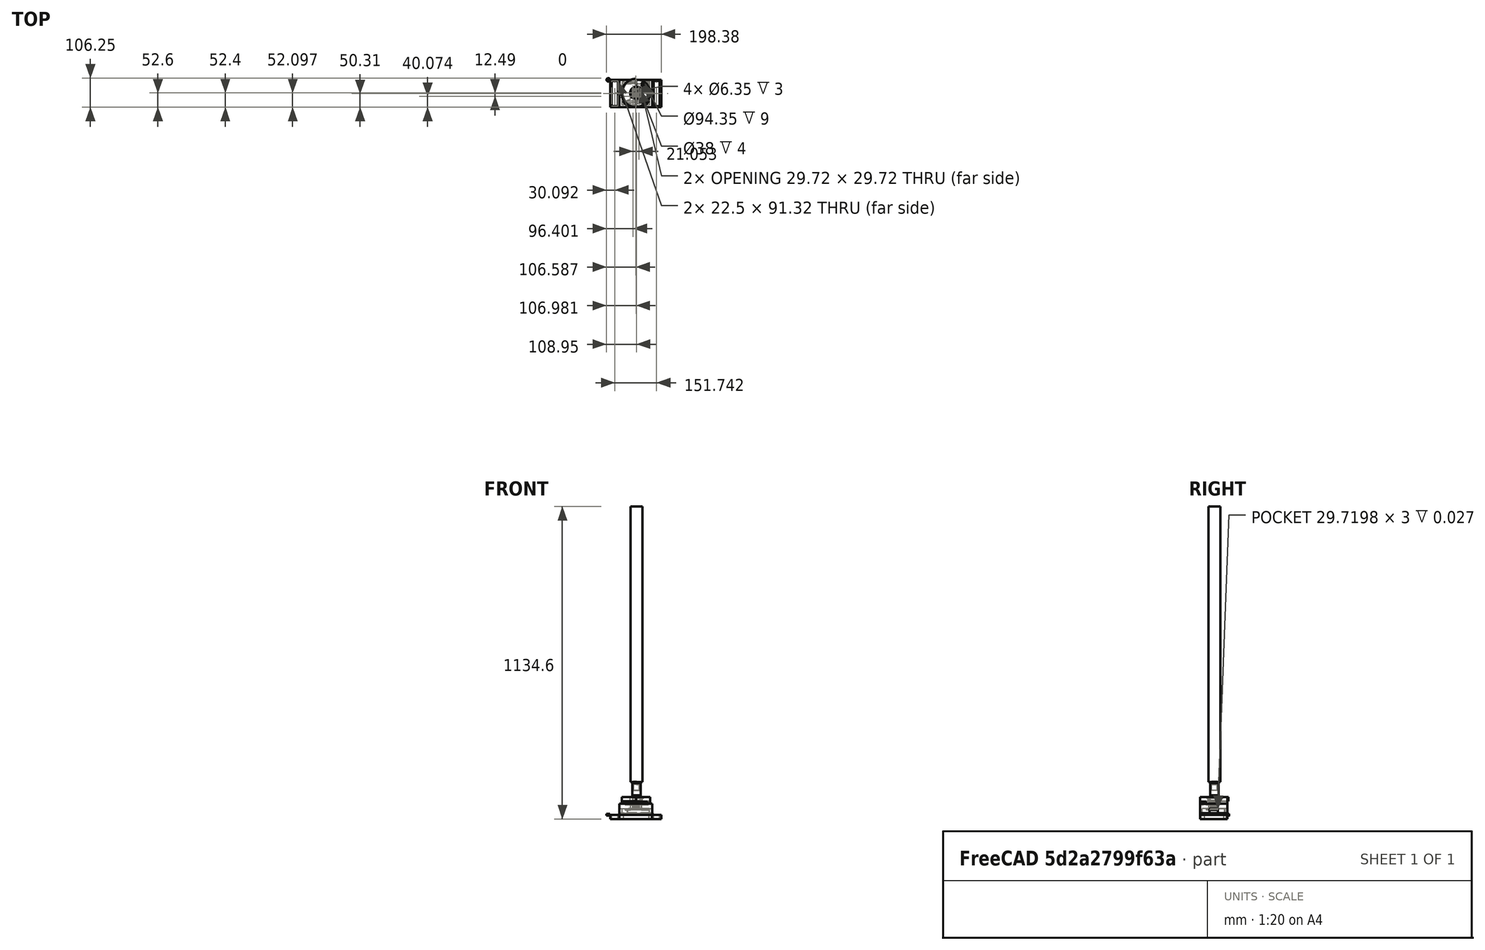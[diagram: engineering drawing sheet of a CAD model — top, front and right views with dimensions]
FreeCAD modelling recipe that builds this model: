
FCSTD DOCUMENT  (FreeCAD 0.20R29603 (Git))
Label: pi_tailtrack_mount
License: All rights reserved
LicenseURL: http://en.wikipedia.org/wiki/All_rights_reserved
objects: Sketcher::SketchObject×43, PartDesign::Pocket×24, PartDesign::Pad×18, Mesh::Feature×13, PartDesign::Body×9, Part::Feature×5, App::MeasureDistance×2, Part::Cut×2, PartDesign::Fillet×1, Part::Compound2×1, PartDesign::FeatureBase×1
note: 146 computed .brp shape members not serialized (recipe doc carries the construction recipe); baked Part::Feature solids carry a one-line shape summary decoded from their .brp

FEATURE [Sketcher::SketchObject] Sketch
  FullyConstrained = false
  MapMode = 5
  Support = -> [XY_Plane]
  sketch-geometry (4):
    g0: LineSegment StartX=0.006331 StartY=0 StartZ=0 EndX=200.006 EndY=0 EndZ=0
    g1: LineSegment StartX=200.006 StartY=0 StartZ=0 EndX=200.006 EndY=-100 EndZ=0
    g2: LineSegment StartX=200.006 StartY=-100 StartZ=0 EndX=0.006331 EndY=-100 EndZ=0
    g3: LineSegment StartX=0.006331 StartY=-100 StartZ=0 EndX=0.006331 EndY=0 EndZ=0
  constraints (13):
    c: Coincident(g0,g1)
    c: Coincident(g1,g2)
    c: Coincident(g2,g3)
    c: Coincident(g3,g0)
    c: Horizontal(g0)
    c: Horizontal(g2)
    c: Vertical(g1)
    c: Vertical(g3)
    c: PointOnObject(g0,g-1)
    c: DistanceX(g0,g0) = 200
    c: DistanceY(g3,g3) = 100
    c: Horizontal(g0,g3)
    c: Horizontal(g3,g-1)
FEATURE [PartDesign::Pad] Pad
  AllowMultiFace = false
  Direction = (0,0,1)
  Length = 6
  Length2 = 100
  Profile = -> Sketch
  Type = 0
FEATURE [Sketcher::SketchObject] Sketch001
  FullyConstrained = false
  MapMode = 5
  Placement = pos=(0,0,6) rot=(0,0,1;0rad)
  Support = -> [Pad]
  sketch-geometry (22):
    g0: LineSegment StartX=0 StartY=0 StartZ=0 EndX=40 EndY=0 EndZ=0
    g1: LineSegment StartX=40 StartY=0 StartZ=0 EndX=40 EndY=-35 EndZ=0
    g2: LineSegment StartX=40 StartY=-35 StartZ=0 EndX=0 EndY=-35 EndZ=0
    g3: LineSegment StartX=0 StartY=-35 StartZ=0 EndX=0 EndY=0 EndZ=0
    g4: LineSegment StartX=0 StartY=-65 StartZ=0 EndX=40 EndY=-65 EndZ=0
    g5: LineSegment StartX=40 StartY=-65 StartZ=0 EndX=40 EndY=-100 EndZ=0
    g6: LineSegment StartX=40 StartY=-100 StartZ=0 EndX=0 EndY=-100 EndZ=0
    g7: LineSegment StartX=0 StartY=-100 StartZ=0 EndX=0 EndY=-65 EndZ=0
    g8: Circle CenterX=19.5564 CenterY=-50 CenterZ=0 NormalX=0 NormalY=0 NormalZ=1 AngleXU=0 Radius=11.9875
    g9: LineSegment StartX=160.311 StartY=0 StartZ=0 EndX=200.311 EndY=0 EndZ=0
    g10: LineSegment StartX=200.311 StartY=0 StartZ=0 EndX=200.311 EndY=-35 EndZ=0
    g11: LineSegment StartX=200.311 StartY=-35 StartZ=0 EndX=160.311 EndY=-35 EndZ=0
    g12: LineSegment StartX=160.311 StartY=-35 StartZ=0 EndX=160.311 EndY=0 EndZ=0
    g13: LineSegment StartX=160.049 StartY=-65 StartZ=0 EndX=200.049 EndY=-65 EndZ=0
    g14: LineSegment StartX=200.049 StartY=-65 StartZ=0 EndX=200.049 EndY=-100 EndZ=0
    g15: LineSegment StartX=200.049 StartY=-100 StartZ=0 EndX=160.049 EndY=-100 EndZ=0
    g16: LineSegment StartX=160.049 StartY=-100 StartZ=0 EndX=160.049 EndY=-65 EndZ=0
    g17: Circle CenterX=179.779 CenterY=-50.3373 CenterZ=0 NormalX=0 NormalY=0 NormalZ=1 AngleXU=0 Radius=11.9875
    g18: LineSegment StartX=53.7678 StartY=-13.6989 StartZ=0 EndX=146 EndY=-13.6989 EndZ=0
    g19: LineSegment StartX=146 StartY=-13.6989 StartZ=0 EndX=146 EndY=-84 EndZ=0
    g20: LineSegment StartX=146 StartY=-84 StartZ=0 EndX=53.7678 EndY=-84 EndZ=0
    g21: LineSegment StartX=53.7678 StartY=-84 StartZ=0 EndX=53.7678 EndY=-13.6989 EndZ=0
  constraints (49):
    c: Coincident(g0,g1)
    c: Coincident(g1,g2)
    c: Coincident(g2,g3)
    c: Coincident(g3,g0)
    c: Horizontal(g0)
    c: Horizontal(g2)
    c: Vertical(g1)
    c: Vertical(g3)
    c: Coincident(g0,g-1)
    c: DistanceX(g0,g0) = 40
    c: DistanceY(g3,g3) = 35
    c: Coincident(g4,g5)
    c: Coincident(g5,g6)
    c: Coincident(g6,g7)
    c: Coincident(g7,g4)
    c: Horizontal(g4)
    c: Horizontal(g6)
    c: Vertical(g5)
    c: Vertical(g7)
    c: Equal(g0,g4) = 40
    c: Equal(g3,g7) = 30
    c: Coincident(g9,g10)
    c: Coincident(g10,g11)
    c: Coincident(g11,g12)
    c: Coincident(g12,g9)
    c: Horizontal(g9)
    c: Horizontal(g11)
    c: Vertical(g10)
    c: Vertical(g12)
    c: Equal(g0,g9) = 40
    c: Equal(g3,g12) = 35
    c: Coincident(g13,g14)
    c: Coincident(g14,g15)
    c: Coincident(g15,g16)
    c: Coincident(g16,g13)
    c: Horizontal(g13)
    c: Horizontal(g15)
    c: Vertical(g14)
    c: Vertical(g16)
    c: Equal(g9,g13) = 40
    c: Equal(g12,g16) = 30
    c: Coincident(g18,g19)
    c: Coincident(g19,g20)
    c: Coincident(g20,g21)
    c: Coincident(g21,g18)
    c: Horizontal(g18)
    c: Horizontal(g20)
    c: Vertical(g19)
    c: Vertical(g21)
FEATURE [PartDesign::Pocket] Pocket
  AllowMultiFace = false
  BaseFeature = -> Pad
  Direction = (1,1,1)
  Length = 6
  Length2 = 100
  Profile = -> Sketch001
  Type = 0
FEATURE [Sketcher::SketchObject] Sketch002
  FullyConstrained = false
  MapMode = 5
  Placement = pos=(0,0,6) rot=(0,0,1;0rad)
  Support = -> [Pocket]
  sketch-geometry (16):
    g0: LineSegment StartX=40 StartY=-35.1993 StartZ=0 EndX=40 EndY=0 EndZ=0
    g1: LineSegment StartX=40 StartY=0 StartZ=0 EndX=160 EndY=0 EndZ=0
    g2: LineSegment StartX=160 StartY=0 StartZ=0 EndX=160 EndY=-35 EndZ=0
    g3: LineSegment StartX=160 StartY=-35 StartZ=0 EndX=149.235 EndY=-35 EndZ=0
    g4: LineSegment StartX=149.235 StartY=-35 StartZ=0 EndX=149.235 EndY=-8.23021 EndZ=0
    g5: LineSegment StartX=149.235 StartY=-8.23021 StartZ=0 EndX=50.0613 EndY=-8.23021 EndZ=0
    g6: LineSegment StartX=50.0613 StartY=-8.23021 StartZ=0 EndX=50.0613 EndY=-35.1993 EndZ=0
    g7: LineSegment StartX=50.0613 StartY=-35.1993 StartZ=0 EndX=40 EndY=-35.1993 EndZ=0
    g8: LineSegment StartX=40 StartY=-100 StartZ=0 EndX=160 EndY=-100 EndZ=0
    g9: LineSegment StartX=160 StartY=-100 StartZ=0 EndX=160 EndY=-65 EndZ=0
    g10: LineSegment StartX=160 StartY=-65 StartZ=0 EndX=149.545 EndY=-65 EndZ=0
    g11: LineSegment StartX=149.545 StartY=-65 StartZ=0 EndX=149.545 EndY=-91.5759 EndZ=0
    g12: LineSegment StartX=149.545 StartY=-91.5759 StartZ=0 EndX=50.3566 EndY=-91.5759 EndZ=0
    g13: LineSegment StartX=50.3566 StartY=-91.5759 StartZ=0 EndX=50.3566 EndY=-65 EndZ=0
    g14: LineSegment StartX=50.3566 StartY=-65 StartZ=0 EndX=40 EndY=-65 EndZ=0
    g15: LineSegment StartX=40 StartY=-65 StartZ=0 EndX=40 EndY=-100 EndZ=0
  constraints (31):
    c: Vertical(g0)
    c: Coincident(g0,g1)
    c: Horizontal(g1)
    c: Coincident(g1,g2)
    c: Vertical(g2)
    c: Coincident(g2,g3)
    c: Horizontal(g3)
    c: Coincident(g3,g4)
    c: Vertical(g4)
    c: Coincident(g4,g5)
    c: Horizontal(g5)
    c: Coincident(g5,g6)
    c: Vertical(g6)
    c: Coincident(g6,g7)
    c: Coincident(g7,g0)
    c: Horizontal(g7)
    c: Horizontal(g8)
    c: Coincident(g8,g9)
    c: Vertical(g9)
    c: Coincident(g9,g10)
    c: Horizontal(g10)
    c: Coincident(g10,g11)
    c: Vertical(g11)
    c: Coincident(g11,g12)
    c: Horizontal(g12)
    c: Coincident(g12,g13)
    c: Vertical(g13)
    c: Coincident(g13,g14)
    c: Coincident(g14,g15)
    c: Coincident(g15,g8)
    c: Vertical(g15)
FEATURE [PartDesign::Pad] Pad001
  AllowMultiFace = false
  BaseFeature = -> Pocket
  Direction = (0,0,1)
  Length = 34
  Length2 = 100
  Profile = -> Sketch002
  Type = 0
FEATURE [Sketcher::SketchObject] Sketch003
  FullyConstrained = false
  MapMode = 5
  Placement = pos=(0,0,40) rot=(0,0,1;0rad)
  Support = -> [Pad001]
  sketch-geometry (4):
    g0: LineSegment StartX=40 StartY=-0.238451 StartZ=0 EndX=160 EndY=-0.238451 EndZ=0
    g1: LineSegment StartX=160 StartY=-0.238451 StartZ=0 EndX=160 EndY=-100 EndZ=0
    g2: LineSegment StartX=160 StartY=-100 StartZ=0 EndX=40 EndY=-100 EndZ=0
    g3: LineSegment StartX=40 StartY=-100 StartZ=0 EndX=40 EndY=-0.238451 EndZ=0
  constraints (8):
    c: Coincident(g0,g1)
    c: Coincident(g1,g2)
    c: Coincident(g2,g3)
    c: Coincident(g3,g0)
    c: Horizontal(g0)
    c: Horizontal(g2)
    c: Vertical(g1)
    c: Vertical(g3)
FEATURE [PartDesign::Pad] Pad002
  AllowMultiFace = false
  BaseFeature = -> Pad001
  Direction = (0,0,1)
  Length = 18
  Length2 = 100
  Profile = -> Sketch003
  Reversed = true
  Type = 0
FEATURE [Sketcher::SketchObject] Sketch004
  FullyConstrained = false
  MapMode = 5
  Placement = pos=(0,0,40) rot=(0,0,1;0rad)
  Support = -> [Pad002]
  sketch-geometry (4):
    g0: LineSegment StartX=82.7298 StartY=-35 StartZ=0 EndX=118.25 EndY=-35 EndZ=0
    g1: LineSegment StartX=118.25 StartY=-35 StartZ=0 EndX=118.25 EndY=-64.9692 EndZ=0
    g2: LineSegment StartX=118.25 StartY=-64.9692 StartZ=0 EndX=82.7298 EndY=-64.9692 EndZ=0
    g3: LineSegment StartX=82.7298 StartY=-64.9692 StartZ=0 EndX=82.7298 EndY=-35 EndZ=0
  constraints (9):
    c: Coincident(g0,g1)
    c: Coincident(g1,g2)
    c: Coincident(g2,g3)
    c: Coincident(g3,g0)
    c: Horizontal(g0)
    c: Horizontal(g2)
    c: Vertical(g1)
    c: Vertical(g3)
    c: DistanceX(g0,g0) = 35.52
FEATURE [PartDesign::Pocket] Pocket001
  AllowMultiFace = false
  BaseFeature = -> Pad002
  Direction = (1,1,1)
  Length = 5
  Length2 = 100
  Profile = -> Sketch004
  Type = 0
FEATURE [Sketcher::SketchObject] Sketch005
  FullyConstrained = false
  MapMode = 5
  Placement = pos=(0,0,35) rot=(0,0,1;0rad)
  Support = -> [Pocket001]
  sketch-geometry (9):
    g0: Circle CenterX=90.1364 CenterY=-47.5 CenterZ=0 NormalX=0 NormalY=0 NormalZ=1 AngleXU=0 Radius=1.5
    g1: Circle CenterX=111.136 CenterY=-47.5 CenterZ=0 NormalX=0 NormalY=0 NormalZ=1 AngleXU=0 Radius=1.5
    g2: Circle CenterX=90.1364 CenterY=-60 CenterZ=0 NormalX=0 NormalY=0 NormalZ=1 AngleXU=0 Radius=1.5
    g3: Circle CenterX=111.136 CenterY=-60 CenterZ=0 NormalX=0 NormalY=0 NormalZ=1 AngleXU=0 Radius=1.5
    g4: LineSegment StartX=105.584 StartY=-52.4517 StartZ=0 EndX=105.588 EndY=-42.5522 EndZ=0
    g5: LineSegment StartX=105.588 StartY=-42.5522 StartZ=0 EndX=95.6887 EndY=-42.5483 EndZ=0
    g6: LineSegment StartX=95.6887 StartY=-42.5483 StartZ=0 EndX=95.6847 EndY=-52.4478 EndZ=0
    g7: LineSegment StartX=95.6847 StartY=-52.4478 StartZ=0 EndX=105.584 EndY=-52.4517 EndZ=0
    g8: Circle CenterX=100.636 CenterY=-47.5 CenterZ=0 NormalX=0 NormalY=0 NormalZ=1 AngleXU=0 Radius=7
  constraints (24):
    c: Radius(g0) = 1.5
    c: Equal(g0,g1) = 2.2
    c: Horizontal(g1,g0)
    c: DistanceX(g0,g1) = 21
    c: Equal(g0,g2) = 2.2
    c: Equal(g2,g3) = 2.2
    c: Horizontal(g3,g2)
    c: DistanceX(g2,g3) = 21
    c: Vertical(g1,g3)
    c: DistanceY(g3,g1) = 12.5
    c: Coincident(g4,g5)
    c: Coincident(g5,g6)
    c: Coincident(g6,g7)
    c: Coincident(g7,g4)
    c: Equal(g4,g5)
    c: Equal(g4,g6)
    c: Equal(g4,g7)
    c: PointOnObject(g4,g8)
    c: PointOnObject(g5,g8)
    c: PointOnObject(g6,g8)
    c: PointOnObject(g7,g8)
    c: Horizontal(g8,g1)
    c: Radius(g8) = 7
    c: DistanceX(g8,g1) = 10.5
FEATURE [PartDesign::Pocket] Pocket002
  AllowMultiFace = false
  BaseFeature = -> Pocket001
  Direction = (1,1,1)
  Length = 20
  Length2 = 100
  Profile = -> Sketch005
  Type = 0
FEATURE [Sketcher::SketchObject] Sketch007
  FullyConstrained = false
  MapMode = 5
  Placement = pos=(0,0,35) rot=(0,0,1;0rad)
  Support = -> [Pocket002]
  sketch-geometry (1):
    g0: Circle CenterX=100.615 CenterY=-47.5274 CenterZ=0 NormalX=0 NormalY=0 NormalZ=1 AngleXU=0 Radius=7
  constraints (1):
    c: Radius(g0) = 7
FEATURE [PartDesign::Pocket] Pocket003
  AllowMultiFace = false
  BaseFeature = -> Pocket002
  Direction = (1,1,1)
  Length = 7
  Length2 = 100
  Profile = -> Sketch007
  Type = 0
FEATURE [Sketcher::SketchObject] Sketch008
  FullyConstrained = false
  MapMode = 5
  Placement = pos=(0,0,0) rot=(0,0.707107,0.707107;3.14159rad)
  Support = -> [Pocket003]
  sketch-geometry (4):
    g0: LineSegment StartX=-150.026 StartY=23.0402 StartZ=0 EndX=-69.393 EndY=23.0402 EndZ=0
    g1: LineSegment StartX=-69.393 StartY=23.0402 StartZ=0 EndX=-69.393 EndY=7.47677 EndZ=0
    g2: LineSegment StartX=-69.393 StartY=7.47677 StartZ=0 EndX=-150.026 EndY=7.47677 EndZ=0
    g3: LineSegment StartX=-150.026 StartY=7.47677 StartZ=0 EndX=-150.026 EndY=23.0402 EndZ=0
  constraints (8):
    c: Coincident(g0,g1)
    c: Coincident(g1,g2)
    c: Coincident(g2,g3)
    c: Coincident(g3,g0)
    c: Horizontal(g0)
    c: Horizontal(g2)
    c: Vertical(g1)
    c: Vertical(g3)
FEATURE [PartDesign::Pocket] Pocket004
  AllowMultiFace = false
  BaseFeature = -> Pocket003
  Direction = (1,1,1)
  Length = 10
  Length2 = 100
  Profile = -> Sketch008
  Type = 0
FEATURE [Sketcher::SketchObject] Sketch015
  FullyConstrained = false
  MapMode = 5
  Placement = pos=(0,0,22) rot=(1,0,0;3.14159rad)
  sketch-geometry (4):
    g0: LineSegment StartX=91.912 StartY=65.7684 StartZ=0 EndX=109.419 EndY=65.7684 EndZ=0
    g1: LineSegment StartX=109.419 StartY=65.7684 StartZ=0 EndX=109.419 EndY=42.0857 EndZ=0
    g2: LineSegment StartX=109.419 StartY=42.0857 StartZ=0 EndX=91.912 EndY=42.0857 EndZ=0
    g3: LineSegment StartX=91.912 StartY=42.0857 StartZ=0 EndX=91.912 EndY=65.7684 EndZ=0
  constraints (8):
    c: Coincident(g0,g1)
    c: Coincident(g1,g2)
    c: Coincident(g2,g3)
    c: Coincident(g3,g0)
    c: Horizontal(g0)
    c: Horizontal(g2)
    c: Vertical(g1)
    c: Vertical(g3)
FEATURE [PartDesign::Pocket] Pocket006
  AllowMultiFace = false
  BaseFeature = -> Pocket004
  Direction = (1,1,1)
  Length = 5
  Length2 = 100
  Profile = -> Sketch015
  Type = 0
FEATURE [Sketcher::SketchObject] Sketch017
  FullyConstrained = false
  MapMode = 5
  Placement = pos=(0,0,40) rot=(0,0,1;0rad)
  Support = -> [Pocket006]
  sketch-geometry (30):
    g0: LineSegment StartX=100.494 StartY=-47.5573 StartZ=0 EndX=59.1615 EndY=-80.1273 EndZ=0
    g1: LineSegment StartX=59.1615 StartY=-80.1273 StartZ=0 EndX=63.9045 EndY=-85.2755 EndZ=0
    g2: LineSegment StartX=63.9045 StartY=-85.2755 StartZ=0 EndX=100.494 EndY=-47.5573 EndZ=0
    g3: LineSegment StartX=100.494 StartY=-47.5573 StartZ=0 EndX=65.7209 EndY=-86.1298 EndZ=0
    g4: LineSegment StartX=65.7209 StartY=-86.1298 StartZ=0 EndX=70.9953 EndY=-90.7321 EndZ=0
    g5: LineSegment StartX=70.9953 StartY=-90.7321 StartZ=0 EndX=100.494 EndY=-47.5573 EndZ=0
    g6: LineSegment StartX=100.469 StartY=-47.6647 StartZ=0 EndX=72.3164 EndY=-91.783 EndZ=0
    g7: LineSegment StartX=72.3164 StartY=-91.783 StartZ=0 EndX=78.3711 EndY=-95.2959 EndZ=0
    g8: LineSegment StartX=78.3711 StartY=-95.2959 StartZ=0 EndX=100.469 EndY=-47.6647 EndZ=0
    g9: LineSegment StartX=100.574 StartY=-47.6121 StartZ=0 EndX=80.8298 EndY=-96.4275 EndZ=0
    g10: LineSegment StartX=80.8298 StartY=-96.4275 StartZ=0 EndX=87.4364 EndY=-98.7413 EndZ=0
    g11: LineSegment StartX=87.4364 StartY=-98.7413 StartZ=0 EndX=100.574 EndY=-47.6121 EndZ=0
    g12: LineSegment StartX=100.574 StartY=-47.6121 StartZ=0 EndX=109.54 EndY=-99.3646 EndZ=0
    g13: LineSegment StartX=109.54 StartY=-99.3646 StartZ=0 EndX=116.439 EndY=-98.178 EndZ=0
    g14: LineSegment StartX=116.439 StartY=-98.178 StartZ=0 EndX=100.574 EndY=-47.6121 EndZ=0
    g15: LineSegment StartX=100.469 StartY=-47.6647 StartZ=0 EndX=100.478 EndY=-100.164 EndZ=0
    g16: LineSegment StartX=100.478 StartY=-100.164 StartZ=0 EndX=107.473 EndY=-99.8814 EndZ=0
    g17: LineSegment StartX=107.473 StartY=-99.8814 StartZ=0 EndX=100.469 EndY=-47.6647 EndZ=0
    g18: LineSegment StartX=100.494 StartY=-47.5573 StartZ=0 EndX=126.724 EndY=-94.2924 EndZ=0
    g19: LineSegment StartX=126.724 StartY=-94.2924 StartZ=0 EndX=132.437 EndY=-90.2469 EndZ=0
    g20: LineSegment StartX=132.437 StartY=-90.2469 StartZ=0 EndX=100.494 EndY=-47.5573 EndZ=0
    g21: LineSegment StartX=100.494 StartY=-47.5573 StartZ=0 EndX=118.389 EndY=-97.4537 EndZ=0
    g22: LineSegment StartX=118.389 StartY=-97.4537 StartZ=0 EndX=124.92 EndY=-94.9352 EndZ=0
    g23: LineSegment StartX=124.92 StartY=-94.9352 StartZ=0 EndX=100.494 EndY=-47.5573 EndZ=0
    g24: LineSegment StartX=100.512 StartY=-47.5427 StartZ=0 EndX=134.392 EndY=-88.2304 EndZ=0
    g25: LineSegment StartX=134.392 StartY=-88.2304 StartZ=0 EndX=139.543 EndY=-83.3947 EndZ=0
    g26: LineSegment StartX=139.543 StartY=-83.3947 StartZ=0 EndX=100.512 EndY=-47.5427 EndZ=0
    g27: LineSegment StartX=100.378 StartY=-47.7964 StartZ=0 EndX=90.0278 EndY=-99.6655 EndZ=0
    g28: LineSegment StartX=97.5884 StartY=-100.124 StartZ=0 EndX=100.378 EndY=-47.7964 EndZ=0
    g29: LineSegment StartX=90.0278 StartY=-99.6655 StartZ=0 EndX=97.5884 EndY=-100.124 EndZ=0
  constraints (35):
    c: Coincident(g0,g1)
    c: Coincident(g1,g2)
    c: Coincident(g2,g0)
    c: Distance(g1) = 7
    c: Coincident(g3,g4)
    c: Coincident(g4,g5)
    c: Coincident(g5,g3)
    c: Equal(g1,g4) = 7
    c: Coincident(g6,g7)
    c: Coincident(g7,g8)
    c: Coincident(g8,g6)
    c: Equal(g1,g7) = 7
    c: Coincident(g9,g10)
    c: Coincident(g10,g11)
    c: Coincident(g11,g9)
    c: Equal(g7,g10) = 7
    c: Coincident(g12,g13)
    c: Coincident(g13,g14)
    c: Coincident(g14,g12)
    c: Coincident(g15,g16)
    c: Coincident(g16,g17)
    c: Coincident(g17,g15)
    c: Coincident(g18,g19)
    c: Coincident(g19,g20)
    c: Coincident(g20,g18)
    c: Equal(g16,g19) = 7
    c: Coincident(g21,g22)
    c: Coincident(g22,g23)
    c: Coincident(g23,g21)
    c: Coincident(g24,g25)
    c: Coincident(g25,g26)
    c: Coincident(g26,g24)
    c: Coincident(g27,g29)
    c: Coincident(g29,g28)
    c: Coincident(g28,g27)
FEATURE [Sketcher::SketchObject] Sketch024
  FullyConstrained = false
  MapMode = 5
  Support = -> [XY_Plane001]
  sketch-geometry (2):
    g0: Circle CenterX=100.523 CenterY=-47.941 CenterZ=0 NormalX=0 NormalY=0 NormalZ=1 AngleXU=0 Radius=51.2787
    g1: Circle CenterX=100.523 CenterY=-47.941 CenterZ=0 NormalX=0 NormalY=0 NormalZ=1 AngleXU=0 Radius=21.439
  constraints (1):
    c: Coincident(g1,g0)
FEATURE [PartDesign::Pad] Pad006
  AllowMultiFace = false
  Direction = (0,0,1)
  Length = 16
  Length2 = 100
  Profile = -> Sketch024
  Type = 0
FEATURE [Sketcher::SketchObject] Sketch025
  FullyConstrained = false
  MapMode = 5
  Placement = pos=(0,0,16) rot=(0,0,1;0rad)
  Support = -> [Pad006]
  sketch-geometry (4):
    g0: LineSegment StartX=100.838 StartY=17.0552 StartZ=0 EndX=167.008 EndY=17.0552 EndZ=0
    g1: LineSegment StartX=167.008 StartY=17.0552 StartZ=0 EndX=167.008 EndY=-112.472 EndZ=0
    g2: LineSegment StartX=167.008 StartY=-112.472 StartZ=0 EndX=100.838 EndY=-112.472 EndZ=0
    g3: LineSegment StartX=100.838 StartY=-112.472 StartZ=0 EndX=100.838 EndY=17.0552 EndZ=0
  constraints (8):
    c: Coincident(g0,g1)
    c: Coincident(g1,g2)
    c: Coincident(g2,g3)
    c: Coincident(g3,g0)
    c: Horizontal(g0)
    c: Horizontal(g2)
    c: Vertical(g1)
    c: Vertical(g3)
FEATURE [PartDesign::Pocket] Pocket011
  AllowMultiFace = false
  BaseFeature = -> Pad006
  Direction = (0,0,-1)
  Length = 16
  Length2 = 100
  Profile = -> Sketch025
  Type = 0
FEATURE [PartDesign::Body] Body001  label="Semicircle"
  Group = -> [Sketch024,Pad006,Sketch025,Pocket011]
  Origin = -> Origin001
  Placement = pos=(0,0,49) rot=(0,0,1;0rad)
  Tip = -> Pocket011
FEATURE [Sketcher::SketchObject] Sketch030
  FullyConstrained = false
  MapMode = 5
  Support = -> [XY_Plane002]
  sketch-geometry (1):
    g0: Circle CenterX=124.126 CenterY=-13.6891 CenterZ=0 NormalX=0 NormalY=0 NormalZ=1 AngleXU=0 Radius=3.26461
FEATURE [PartDesign::Pad] Pad009
  AllowMultiFace = false
  Direction = (1,1,1)
  Length = 50
  Length2 = 100
  Profile = -> Sketch030
  Type = 0
FEATURE [PartDesign::Body] Body002  label="LeftEyeCut"
  Group = -> [Sketch030,Pad009]
  Origin = -> Origin002
  Placement = pos=(2,-5,98) rot=(-0.707107,0.707107,0;0.785398rad)
  Tip = -> Pad009
FEATURE [Sketcher::SketchObject] Sketch031
  FullyConstrained = false
  MapMode = 5
  Support = -> [XY_Plane003]
  sketch-geometry (1):
    g0: Circle CenterX=124.126 CenterY=-13.6891 CenterZ=0 NormalX=0 NormalY=0 NormalZ=1 AngleXU=0 Radius=3.26461
FEATURE [PartDesign::Pad] Pad010
  AllowMultiFace = false
  Direction = (1,1,1)
  Length = 50
  Length2 = 100
  Profile = -> Sketch031
  Type = 0
FEATURE [PartDesign::Body] Body003  label="RigthEyeCut"
  Group = -> [Sketch031,Pad010]
  Origin = -> Origin003
  Placement = pos=(6,-65,112) rot=(0.707107,0.707107,0;0.785398rad)
  Tip = -> Pad010
FEATURE [Sketcher::SketchObject] Sketch032
  FullyConstrained = false
  MapMode = 5
  Support = -> [XY_Plane004]
  sketch-geometry (4):
    g0: LineSegment StartX=82.7935 StartY=-35.0406 StartZ=0 EndX=118.134 EndY=-35.0406 EndZ=0
    g1: LineSegment StartX=118.134 StartY=-35.0406 StartZ=0 EndX=118.134 EndY=-64.7316 EndZ=0
    g2: LineSegment StartX=118.134 StartY=-64.7316 StartZ=0 EndX=82.7935 EndY=-64.7316 EndZ=0
    g3: LineSegment StartX=82.7935 StartY=-64.7316 StartZ=0 EndX=82.7935 EndY=-35.0406 EndZ=0
  constraints (8):
    c: Coincident(g0,g1)
    c: Coincident(g1,g2)
    c: Coincident(g2,g3)
    c: Coincident(g3,g0)
    c: Horizontal(g0)
    c: Horizontal(g2)
    c: Vertical(g1)
    c: Vertical(g3)
FEATURE [PartDesign::Pad] Pad011
  AllowMultiFace = false
  Direction = (1,1,1)
  Length = 5
  Length2 = 100
  Profile = -> Sketch032
  Type = 0
FEATURE [Sketcher::SketchObject] Sketch033
  FullyConstrained = false
  MapMode = 5
  Placement = pos=(0,0,0) rot=(1,0,0;3.14159rad)
  Support = -> [Pad011]
  sketch-geometry (4):
    g0: Circle CenterX=90.1511 CenterY=59.9051 CenterZ=0 NormalX=0 NormalY=0 NormalZ=1 AngleXU=0 Radius=3.17621
    g1: Circle CenterX=90.237 CenterY=47.4366 CenterZ=0 NormalX=0 NormalY=0 NormalZ=1 AngleXU=0 Radius=3.17621
    g2: Circle CenterX=111.204 CenterY=59.9265 CenterZ=0 NormalX=0 NormalY=0 NormalZ=1 AngleXU=0 Radius=3.17621
    g3: Circle CenterX=111.204 CenterY=47.501 CenterZ=0 NormalX=0 NormalY=0 NormalZ=1 AngleXU=0 Radius=3.17621
FEATURE [PartDesign::Pocket] Pocket014
  AllowMultiFace = false
  BaseFeature = -> Pad011
  Direction = (1,1,1)
  Length = 3
  Length2 = 100
  Profile = -> Sketch033
  Type = 0
FEATURE [Sketcher::SketchObject] Sketch034
  FullyConstrained = false
  MapMode = 5
  Placement = pos=(0,0,0) rot=(1,0,0;3.14159rad)
  Support = -> [Pocket014]
  sketch-geometry (1):
    g0: Circle CenterX=100.582 CenterY=47.4887 CenterZ=0 NormalX=0 NormalY=0 NormalZ=1 AngleXU=0 Radius=7
  constraints (1):
    c: Diameter(g0) = 14
FEATURE [PartDesign::Pocket] Pocket015
  AllowMultiFace = false
  BaseFeature = -> Pocket014
  Direction = (1,1,1)
  Length = 5
  Length2 = 100
  Profile = -> Sketch034
  Type = 0
FEATURE [PartDesign::Body] Body004  label="CameraDepressionInsert"
  Group = -> [Sketch032,Pad011,Sketch033,Pocket014,Sketch034,Pocket015]
  Origin = -> Origin004
  Placement = pos=(0,0,35) rot=(0,0,1;0rad)
  Tip = -> Pocket015
FEATURE [Part::Feature] Part__Feature  label="Cam V2.1 v1"
  Placement = pos=(100.6,-50,21) rot=(0.707107,0,0.707107;3.14159rad)
  shape: bbox 25 x 24 x 6.45 mm, 247 faces (baked)
FEATURE [Mesh::Feature] LED_5mm  label="Red_LED_1"
  Placement = pos=(135.001,0.727905,87.6792) rot=(0.962528,-0.0838,-0.257909;2.53538rad)
FEATURE [Mesh::Feature] LED_5mm001  label="Red_LED_2"
  Placement = pos=(133.359,-85.3415,94.0713) rot=(0.948002,-0.161603,-0.274184;3.58891rad)
FEATURE [Mesh::Feature] LED_5mm002  label="IR_LED"
  Placement = pos=(154.892,-115.515,46.8) rot=(-0.873594,-0.344118,0.344118;1.70553rad)
FEATURE [Mesh::Feature] LED_5mm003  label="IR_LED001"
  Placement = pos=(142.243,-124.48,46.8) rot=(-0.922341,-0.27321,0.27321;1.65155rad)
FEATURE [Mesh::Feature] LED_5mm004  label="IR_LED002"
  Placement = pos=(128.505,-130.552,46.8) rot=(-0.961012,-0.19552,0.19552;1.61055rad)
FEATURE [Mesh::Feature] LED_5mm005  label="IR_LED003"
  Placement = pos=(114.514,-134.49,46.8) rot=(-0.985257,-0.120974,0.120974;1.58565rad)
FEATURE [Mesh::Feature] LED_5mm006  label="IR_LED004"
  Placement = pos=(99.6109,-135.395,46.8) rot=(-0.998783,-0.034878,0.034878;1.57201rad)
FEATURE [Mesh::Feature] LED_5mm007  label="IR_LED005"
  Placement = pos=(82.8154,-133.75,46.8) rot=(-0.99628,0.060935,-0.060935;1.57452rad)
FEATURE [Mesh::Feature] LED_5mm008  label="IR_LED006"
  Placement = pos=(64.7966,-127.636,46.8) rot=(-0.967324,0.179283,-0.179283;1.60401rad)
FEATURE [Mesh::Feature] LED_5mm009  label="IR_LED007"
  Placement = pos=(51.4171,-120.378,46.8) rot=(-0.935113,0.250563,-0.250563;1.63783rad)
FEATURE [Mesh::Feature] LED_5mm010  label="IR_LED008"
  Placement = pos=(40.3946,-111.928,46.8) rot=(-0.894141,0.316632,-0.316632;1.68246rad)
FEATURE [Mesh::Feature] LED_5mm011  label="IR_LED009"
  Placement = pos=(30.1096,-100.339,46.8) rot=(-0.834817,0.389282,-0.389282;1.75037rad)
FEATURE [Part::Feature] Part__Feature001  label="TTN031489-E0W"
  Placement = pos=(102.7,-47.4,82.1) rot=(0,1,0;1.5708rad)
  shape: bbox 29.97 x 29.97 x 78.87 mm, 81 faces (baked)
FEATURE [Mesh::Feature] Zebrafish_6dpf_actualActualSize  label="Zebrafish-6dpf-actualActualSize"
  Placement = pos=(102.4,-47.5,41.6) rot=(0.57735,0.57735,0.57735;2.0944rad)
FEATURE [Sketcher::SketchObject] Sketch035
  FullyConstrained = false
  MapMode = 5
  Support = -> [XY_Plane005]
  sketch-geometry (1):
    g0: Circle CenterX=100.659 CenterY=-47.5423 CenterZ=0 NormalX=0 NormalY=0 NormalZ=1 AngleXU=0 Radius=20
  constraints (1):
    c: Diameter(g0) = 40
FEATURE [PartDesign::Pad] Pad012
  Direction = (0,0,1)
  Length = 1
  Length2 = 10
  Profile = -> Sketch035
  Type = 0
FEATURE [Sketcher::SketchObject] Sketch036
  FullyConstrained = false
  MapMode = 5
  Placement = pos=(0,0,1) rot=(0,0,1;0rad)
  Support = -> [Pad012]
  sketch-geometry (2):
    g0: Circle CenterX=100.731 CenterY=-47.6003 CenterZ=0 NormalX=0 NormalY=0 NormalZ=1 AngleXU=0 Radius=20
    g1: Circle CenterX=100.731 CenterY=-47.6003 CenterZ=0 NormalX=0 NormalY=0 NormalZ=1 AngleXU=0 Radius=19
  constraints (3):
    c: Diameter(g0) = 40
    c: Coincident(g1,g0)
    c: Diameter(g1) = 38
FEATURE [PartDesign::Pad] Pad013
  BaseFeature = -> Pad012
  Direction = (0,0,1)
  Length = 4
  Length2 = 10
  Profile = -> Sketch036
  Type = 0
FEATURE [PartDesign::Body] Body005  label="40mm_dish"
  Group = -> [Sketch035,Pad012,Sketch036,Pad013]
  Origin = -> Origin005
  Placement = pos=(0,0,40) rot=(0,0,1;0rad)
  Tip = -> Pad013
FEATURE [Sketcher::SketchObject] Sketch037
  FullyConstrained = false
  MapMode = 5
  Support = -> [XY_Plane006]
  sketch-geometry (1):
    g0: Circle CenterX=102.61 CenterY=-47.5813 CenterZ=0 NormalX=0 NormalY=0 NormalZ=1 AngleXU=0 Radius=7.5
  constraints (1):
    c: Diameter(g0) = 15
FEATURE [PartDesign::Pad] Pad014
  Direction = (0,0,1)
  Length = 2
  Length2 = 10
  Profile = -> Sketch037
  Type = 0
FEATURE [PartDesign::Fillet] Fillet
  Base = -> Pad014 [Face3]
  BaseFeature = -> Pad014
  Radius = 1.9
  SupportTransform = false
  UseAllEdges = false
FEATURE [Sketcher::SketchObject] Sketch038
  FullyConstrained = false
  MapMode = 5
  Placement = pos=(0,0,2) rot=(0,0,1;0rad)
  Support = -> [Fillet]
  sketch-geometry (4):
    g0: LineSegment StartX=93.544 StartY=-43.374 StartZ=0 EndX=101.094 EndY=-43.374 EndZ=0
    g1: LineSegment StartX=101.094 StartY=-43.374 StartZ=0 EndX=101.094 EndY=-52.0559 EndZ=0
    g2: LineSegment StartX=101.094 StartY=-52.0559 StartZ=0 EndX=93.544 EndY=-52.0559 EndZ=0
    g3: LineSegment StartX=93.544 StartY=-52.0559 StartZ=0 EndX=93.544 EndY=-43.374 EndZ=0
  constraints (8):
    c: Coincident(g0,g1)
    c: Coincident(g1,g2)
    c: Coincident(g2,g3)
    c: Coincident(g3,g0)
    c: Horizontal(g0)
    c: Horizontal(g2)
    c: Vertical(g1)
    c: Vertical(g3)
FEATURE [PartDesign::Pocket] Pocket016
  BaseFeature = -> Fillet
  Direction = (1,1,1)
  Length = 5
  Length2 = 5
  Profile = -> Sketch038
  Type = 0
FEATURE [PartDesign::Body] Body006  label="Agarose_block"
  Group = -> [Sketch037,Pad014,Fillet,Sketch038,Pocket016]
  Origin = -> Origin006
  Placement = pos=(0,0,40) rot=(0,0,1;0rad)
  Tip = -> Pocket016
FEATURE [Sketcher::SketchObject] Sketch039
  FullyConstrained = false
  MapMode = 5
  Support = -> [XY_Plane007]
  sketch-geometry (1):
    g0: Circle CenterX=102.568 CenterY=-47.0303 CenterZ=0 NormalX=0 NormalY=0 NormalZ=1 AngleXU=0 Radius=21.6315
FEATURE [PartDesign::Pad] Pad015
  Direction = (0,0,1)
  Length = 1000
  Length2 = 10
  Profile = -> Sketch039
  Type = 0
FEATURE [PartDesign::Body] Body007  label="MicroscopeTube"
  Group = -> [Sketch039,Pad015]
  Origin = -> Origin007
  Placement = pos=(0,0,119.6) rot=(0,0,1;0rad)
  Tip = -> Pad015
FEATURE [Part::Feature] Solid002
  shape: bbox 12.5 x 12.5 x 5.9 mm, 9 faces (baked)
FEATURE [Part::Feature] Solid003
  shape: bbox 11 x 11 x 4.9 mm, 4 faces (baked)
FEATURE [Part::Compound2] Compound001  label="ֱ2_67789"
  Links = -> [Solid002,Solid003]
  Placement = pos=(100.8,-47.5,31) rot=(0,0,1;0rad)
FEATURE [App::MeasureDistance] Distance001  label="Distance: 21.02 mm"
  Distance = 21.0166
  P1 = (101.152,-47.5357,21)
  P2 = (101.976,-47.3996,42)
FEATURE [App::MeasureDistance] Distance  label="Distance: 21.84 mm"
  Distance = 21.8362
  P1 = (102.748,-48.2468,42.6665)
  P2 = (100.164,-47.408,21)
FEATURE [Part::Feature] Cut001001  label="MainShape001"
  shape: bbox 185 x 100 x 84.87 mm, 221 faces (baked)
FEATURE [PartDesign::FeatureBase] BaseFeature
  BaseFeature = -> Cut001001
FEATURE [Sketcher::SketchObject] Sketch040
  FullyConstrained = false
  MapMode = 5
  Placement = pos=(160,0,0) rot=(0.57735,0.57735,0.57735;2.0944rad)
  Support = -> [BaseFeature]
  sketch-geometry (6):
    g0: LineSegment StartX=-107.574 StartY=48.016 StartZ=0 EndX=-77.9169 EndY=48.016 EndZ=0
    g1: LineSegment StartX=-77.9169 StartY=48.016 StartZ=0 EndX=-77.9169 EndY=39.9391 EndZ=0
    g2: LineSegment StartX=-77.9169 StartY=39.9391 StartZ=0 EndX=19.6203 EndY=39.9391 EndZ=0
    g3: LineSegment StartX=19.6203 StartY=39.9391 StartZ=0 EndX=18.0104 EndY=73.5036 EndZ=0
    g4: LineSegment StartX=18.0104 StartY=73.5036 StartZ=0 EndX=-106.75 EndY=73.5036 EndZ=0
    g5: LineSegment StartX=-106.75 StartY=73.5036 StartZ=0 EndX=-107.574 EndY=48.016 EndZ=0
  constraints (10):
    c: Horizontal(g0)
    c: Coincident(g0,g1)
    c: Vertical(g1)
    c: Coincident(g1,g2)
    c: Horizontal(g2)
    c: Coincident(g2,g3)
    c: Coincident(g3,g4)
    c: Horizontal(g4)
    c: Coincident(g4,g5)
    c: Coincident(g5,g0)
FEATURE [PartDesign::Pocket] Pocket017
  BaseFeature = -> BaseFeature
  Direction = (-1,0,0)
  Length = 2000
  Length2 = 5
  Profile = -> Sketch040
  ReferenceAxis = -> Sketch040 [N_Axis]
  Type = 0
FEATURE [Sketcher::SketchObject] Sketch041
  FullyConstrained = false
  MapMode = 5
  Placement = pos=(0,0,39.9391) rot=(0,0,1;0rad)
  Support = -> [Pocket017]
  sketch-geometry (8):
    g0: LineSegment StartX=61 StartY=-28 StartZ=0 EndX=146 EndY=-28 EndZ=0
    g1: LineSegment StartX=146 StartY=-28 StartZ=0 EndX=146 EndY=-99 EndZ=0
    g2: LineSegment StartX=146 StartY=-99 StartZ=0 EndX=61 EndY=-99 EndZ=0
    g3: LineSegment StartX=61 StartY=-99 StartZ=0 EndX=61 EndY=-28 EndZ=0
    g4: LineSegment StartX=-59 StartY=61 StartZ=0 EndX=235.477 EndY=61 EndZ=0
    g5: LineSegment StartX=235.477 StartY=61 StartZ=0 EndX=235.477 EndY=-120.201 EndZ=0
    g6: LineSegment StartX=235.477 StartY=-120.201 StartZ=0 EndX=-59 EndY=-120.201 EndZ=0
    g7: LineSegment StartX=-59 StartY=-120.201 StartZ=0 EndX=-59 EndY=61 EndZ=0
  constraints (16):
    c: Coincident(g0,g1)
    c: Coincident(g1,g2)
    c: Coincident(g2,g3)
    c: Coincident(g3,g0)
    c: Horizontal(g0)
    c: Horizontal(g2)
    c: Vertical(g1)
    c: Vertical(g3)
    c: Coincident(g4,g5)
    c: Coincident(g5,g6)
    c: Coincident(g6,g7)
    c: Coincident(g7,g4)
    c: Horizontal(g4)
    c: Horizontal(g6)
    c: Vertical(g5)
    c: Vertical(g7)
FEATURE [PartDesign::Pocket] Pocket018
  BaseFeature = -> Pocket017
  Direction = (0,0,-1)
  Length = 500
  Length2 = 5
  Profile = -> Sketch041
  ReferenceAxis = -> Sketch041 [N_Axis]
  Type = 0
FEATURE [Sketcher::SketchObject] Sketch042
  FullyConstrained = false
  MapMode = 5
  Placement = pos=(61,0,0) rot=(0.57735,-0.57735,-0.57735;2.0944rad)
  Support = -> [Pocket018]
  sketch-geometry (4):
    g0: LineSegment StartX=71 StartY=36 StartZ=0 EndX=102.279 EndY=36 EndZ=0
    g1: LineSegment StartX=102.279 StartY=36 StartZ=0 EndX=102.279 EndY=-17.0189 EndZ=0
    g2: LineSegment StartX=102.279 StartY=-17.0189 StartZ=0 EndX=71 EndY=-17.0189 EndZ=0
    g3: LineSegment StartX=71 StartY=-17.0189 StartZ=0 EndX=71 EndY=36 EndZ=0
  constraints (8):
    c: Coincident(g0,g1)
    c: Coincident(g1,g2)
    c: Coincident(g2,g3)
    c: Coincident(g3,g0)
    c: Horizontal(g0)
    c: Horizontal(g2)
    c: Vertical(g1)
    c: Vertical(g3)
FEATURE [PartDesign::Pocket] Pocket019
  BaseFeature = -> Pocket018
  Direction = (1,0,0)
  Length = 500
  Length2 = 5
  Profile = -> Sketch042
  ReferenceAxis = -> Sketch042 [N_Axis]
  Type = 0
FEATURE [Sketcher::SketchObject] Sketch043
  FullyConstrained = false
  MapMode = 5
  Placement = pos=(0,0,22) rot=(1,0,0;3.14159rad)
  Support = -> [Pocket019]
  sketch-geometry (2):
    g0: Circle CenterX=100.496 CenterY=48 CenterZ=0 NormalX=0 NormalY=0 NormalZ=1 AngleXU=0 Radius=55.989
    g1: Circle CenterX=90.6006 CenterY=53.3713 CenterZ=0 NormalX=0 NormalY=0 NormalZ=1 AngleXU=0 Radius=183.683
FEATURE [PartDesign::Pocket] Pocket020
  BaseFeature = -> Pocket019
  Direction = (0,0,1)
  Length = 500
  Length2 = 5
  Profile = -> Sketch043
  ReferenceAxis = -> Sketch043 [N_Axis]
  Type = 0
FEATURE [Sketcher::SketchObject] Sketch044
  FullyConstrained = false
  MapMode = 5
  Placement = pos=(0,0,22) rot=(1,0,0;3.14159rad)
  Support = -> [Pocket020]
  sketch-geometry (8):
    g0: LineSegment StartX=82.9733 StartY=64.779 StartZ=0 EndX=118.048 EndY=64.779 EndZ=0
    g1: LineSegment StartX=118.048 StartY=64.779 StartZ=0 EndX=118.048 EndY=35.0592 EndZ=0
    g2: LineSegment StartX=118.048 StartY=35.0592 StartZ=0 EndX=82.9733 EndY=35.0592 EndZ=0
    g3: LineSegment StartX=82.9733 StartY=35.0592 StartZ=0 EndX=82.9733 EndY=64.779 EndZ=0
    g4: LineSegment StartX=146 StartY=27.6028 StartZ=0 EndX=60.9208 EndY=27.6028 EndZ=0
    g5: LineSegment StartX=60.9208 StartY=27.6028 StartZ=0 EndX=60.9208 EndY=77.9095 EndZ=0
    g6: LineSegment StartX=60.9208 StartY=77.9095 StartZ=0 EndX=146 EndY=77.9095 EndZ=0
    g7: LineSegment StartX=146 StartY=77.9095 StartZ=0 EndX=146 EndY=27.6028 EndZ=0
  constraints (16):
    c: Coincident(g0,g1)
    c: Coincident(g1,g2)
    c: Coincident(g2,g3)
    c: Coincident(g3,g0)
    c: Horizontal(g0)
    c: Horizontal(g2)
    c: Vertical(g1)
    c: Vertical(g3)
    c: Coincident(g4,g5)
    c: Coincident(g5,g6)
    c: Coincident(g6,g7)
    c: Coincident(g7,g4)
    c: Horizontal(g4)
    c: Horizontal(g6)
    c: Vertical(g5)
    c: Vertical(g7)
FEATURE [PartDesign::Pad] Pad016
  BaseFeature = -> Pocket020
  Direction = (0,0,-1)
  Length = 3
  Length2 = 10
  Profile = -> Sketch044
  ReferenceAxis = -> Sketch044 [N_Axis]
  Type = 0
FEATURE [Sketcher::SketchObject] Sketch045
  FullyConstrained = false
  MapMode = 5
  Placement = pos=(0,-28,0) rot=(0,0.707107,0.707107;3.14159rad)
  Support = -> [Pad016]
  sketch-geometry (4):
    g0: LineSegment StartX=-107.609 StartY=34.5723 StartZ=0 EndX=-93.5937 EndY=34.5723 EndZ=0
    g1: LineSegment StartX=-93.5937 StartY=34.5723 StartZ=0 EndX=-93.5937 EndY=27.9882 EndZ=0
    g2: LineSegment StartX=-93.5937 StartY=27.9882 StartZ=0 EndX=-107.609 EndY=27.9882 EndZ=0
    g3: LineSegment StartX=-107.609 StartY=27.9882 StartZ=0 EndX=-107.609 EndY=34.5723 EndZ=0
  constraints (8):
    c: Coincident(g0,g1)
    c: Coincident(g1,g2)
    c: Coincident(g2,g3)
    c: Coincident(g3,g0)
    c: Horizontal(g0)
    c: Horizontal(g2)
    c: Vertical(g1)
    c: Vertical(g3)
FEATURE [PartDesign::Pocket] Pocket021
  BaseFeature = -> Pad016
  Direction = (0,-1,2e-16)
  Length = 26.5
  Length2 = 5
  Profile = -> Sketch045
  ReferenceAxis = -> Sketch045 [N_Axis]
  Type = 0
FEATURE [Sketcher::SketchObject] Sketch046
  FullyConstrained = false
  MapMode = 5
  Placement = pos=(0,0,39.9391) rot=(0,0,1;0rad)
  Support = -> [Pocket021]
  sketch-geometry (8):
    g0: LineSegment StartX=81.3487 StartY=-32.8528 StartZ=0 EndX=120.368 EndY=-32.8528 EndZ=0
    g1: LineSegment StartX=120.368 StartY=-32.8528 StartZ=0 EndX=120.368 EndY=-66.6113 EndZ=0
    g2: LineSegment StartX=120.368 StartY=-66.6113 StartZ=0 EndX=81.3487 EndY=-66.6113 EndZ=0
    g3: LineSegment StartX=81.3487 StartY=-66.6113 StartZ=0 EndX=81.3487 EndY=-32.8528 EndZ=0
    g4: Circle CenterX=90.1046 CenterY=-47.5388 CenterZ=0 NormalX=0 NormalY=0 NormalZ=1 AngleXU=0 Radius=3
    g5: Circle CenterX=111.145 CenterY=-47.5905 CenterZ=0 NormalX=0 NormalY=0 NormalZ=1 AngleXU=0 Radius=3
    g6: Circle CenterX=111.057 CenterY=-60.0856 CenterZ=0 NormalX=0 NormalY=0 NormalZ=1 AngleXU=0 Radius=3
    g7: Circle CenterX=90.1006 CenterY=-60.0856 CenterZ=0 NormalX=0 NormalY=0 NormalZ=1 AngleXU=0 Radius=3
  constraints (12):
    c: Coincident(g0,g1)
    c: Coincident(g1,g2)
    c: Coincident(g2,g3)
    c: Coincident(g3,g0)
    c: Horizontal(g0)
    c: Horizontal(g2)
    c: Vertical(g1)
    c: Vertical(g3)
    c: Diameter(g4) = 6
    c: Diameter(g5) = 6
    c: Diameter(g6) = 6
    c: Diameter(g7) = 6
FEATURE [PartDesign::Pad] Pad017
  BaseFeature = -> Pocket021
  Direction = (0,0,1)
  Length = 5
  Length2 = 10
  Profile = -> Sketch046
  ReferenceAxis = -> Sketch046 [N_Axis]
  Reversed = true
  Type = 0
FEATURE [Sketcher::SketchObject] Sketch047
  FullyConstrained = false
  MapMode = 5
  Placement = pos=(0,0,19) rot=(1,0,0;3.14159rad)
  Support = -> [Pad017]
  sketch-geometry (8):
    g0: LineSegment StartX=60.7995 StartY=78 StartZ=0 EndX=81 EndY=70 EndZ=0
    g1: LineSegment StartX=81 StartY=70 StartZ=0 EndX=81 EndY=34.7636 EndZ=0
    g2: LineSegment StartX=81 StartY=34.7636 StartZ=0 EndX=120 EndY=34.7636 EndZ=0
    g3: LineSegment StartX=120 StartY=34.7636 StartZ=0 EndX=120 EndY=70 EndZ=0
    g4: LineSegment StartX=120 StartY=70 StartZ=0 EndX=146 EndY=78 EndZ=0
    g5: LineSegment StartX=146 StartY=78 StartZ=0 EndX=179.505 EndY=-1.6033 EndZ=0
    g6: LineSegment StartX=179.505 StartY=-1.6033 StartZ=0 EndX=22.5169 EndY=-1.6033 EndZ=0
    g7: LineSegment StartX=22.5169 StartY=-1.6033 StartZ=0 EndX=60.7995 EndY=78 EndZ=0
  constraints (11):
    c: Coincident(g0,g1)
    c: Vertical(g1)
    c: Coincident(g1,g2)
    c: Horizontal(g2)
    c: Coincident(g2,g3)
    c: Coincident(g3,g4)
    c: Coincident(g4,g5)
    c: Coincident(g5,g6)
    c: Horizontal(g6)
    c: Coincident(g6,g7)
    c: Coincident(g7,g0)
FEATURE [PartDesign::Pocket] Pocket022
  BaseFeature = -> Pad017
  Direction = (0,0,1)
  Length = 200
  Length2 = 5
  Profile = -> Sketch047
  ReferenceAxis = -> Sketch047 [N_Axis]
  Type = 0
FEATURE [Sketcher::SketchObject] Sketch048
  FullyConstrained = false
  MapMode = 5
  Placement = pos=(0,0,19) rot=(1,0,0;3.14159rad)
  Support = -> [Pocket022]
  sketch-geometry (4):
    g0: LineSegment StartX=57.745 StartY=84.0181 StartZ=0 EndX=148.655 EndY=84.0181 EndZ=0
    g1: LineSegment StartX=148.655 StartY=84.0181 StartZ=0 EndX=148.655 EndY=70.5972 EndZ=0
    g2: LineSegment StartX=148.655 StartY=70.5972 StartZ=0 EndX=57.745 EndY=70.5972 EndZ=0
    g3: LineSegment StartX=57.745 StartY=70.5972 StartZ=0 EndX=57.745 EndY=84.0181 EndZ=0
  constraints (8):
    c: Coincident(g0,g1)
    c: Coincident(g1,g2)
    c: Coincident(g2,g3)
    c: Coincident(g3,g0)
    c: Horizontal(g0)
    c: Horizontal(g2)
    c: Vertical(g1)
    c: Vertical(g3)
FEATURE [PartDesign::Pocket] Pocket023
  BaseFeature = -> Pocket022
  Direction = (0,0,1)
  Length = 5
  Length2 = 5
  Profile = -> Sketch048
  ReferenceAxis = -> Sketch048 [N_Axis]
  Type = 0
FEATURE [Sketcher::SketchObject] Sketch049
  FullyConstrained = false
  MapMode = 5
  Placement = pos=(0,0,19) rot=(1,0,0;3.14159rad)
  Support = -> [Pocket023]
  sketch-geometry (4):
    g0: LineSegment StartX=77.3301 StartY=72.8516 StartZ=0 EndX=124.899 EndY=72.8516 EndZ=0
    g1: LineSegment StartX=124.899 StartY=72.8516 StartZ=0 EndX=124.899 EndY=69.3443 EndZ=0
    g2: LineSegment StartX=124.899 StartY=69.3443 StartZ=0 EndX=77.3301 EndY=69.3443 EndZ=0
    g3: LineSegment StartX=77.3301 StartY=69.3443 StartZ=0 EndX=77.3301 EndY=72.8516 EndZ=0
  constraints (8):
    c: Coincident(g0,g1)
    c: Coincident(g1,g2)
    c: Coincident(g2,g3)
    c: Coincident(g3,g0)
    c: Horizontal(g0)
    c: Horizontal(g2)
    c: Vertical(g1)
    c: Vertical(g3)
FEATURE [PartDesign::Pocket] Pocket024
  BaseFeature = -> Pocket023
  Direction = (0,0,1)
  Length = 17
  Length2 = 5
  Profile = -> Sketch049
  ReferenceAxis = -> Sketch049 [N_Axis]
  Type = 0
FEATURE [Sketcher::SketchObject] Sketch050
  FullyConstrained = false
  MapMode = 5
  Placement = pos=(0,0,19) rot=(1,0,0;3.14159rad)
  Support = -> [Pocket024]
  sketch-geometry (10):
    g0: LineSegment StartX=120 StartY=70 StartZ=0 EndX=120 EndY=34.6601 EndZ=0
    g1: LineSegment StartX=120 StartY=34.6601 StartZ=0 EndX=118 EndY=34.6601 EndZ=0
    g2: LineSegment StartX=118 StartY=34.6601 StartZ=0 EndX=118 EndY=65 EndZ=0
    g3: LineSegment StartX=118 StartY=65 StartZ=0 EndX=83 EndY=65 EndZ=0
    g4: LineSegment StartX=83 StartY=65 StartZ=0 EndX=83 EndY=34.7758 EndZ=0
    g5: LineSegment StartX=83 StartY=34.7758 StartZ=0 EndX=81 EndY=34.7758 EndZ=0
    g6: LineSegment StartX=81 StartY=34.7758 StartZ=0 EndX=81 EndY=70 EndZ=0
    g7: LineSegment StartX=120 StartY=70 StartZ=0 EndX=145.775 EndY=78 EndZ=0
    g8: LineSegment StartX=145.775 StartY=78 StartZ=0 EndX=61 EndY=78 EndZ=0
    g9: LineSegment StartX=61 StartY=78 StartZ=0 EndX=81 EndY=70 EndZ=0
  constraints (18):
    c: Vertical(g0)
    c: Coincident(g0,g1)
    c: Horizontal(g1)
    c: Coincident(g1,g2)
    c: Vertical(g2)
    c: Coincident(g2,g3)
    c: Horizontal(g3)
    c: Coincident(g3,g4)
    c: Vertical(g4)
    c: Coincident(g4,g5)
    c: Horizontal(g5)
    c: Coincident(g5,g6)
    c: Vertical(g6)
    c: Coincident(g0,g7)
    c: Coincident(g7,g8)
    c: Horizontal(g8)
    c: Coincident(g8,g9)
    c: Coincident(g9,g6)
FEATURE [PartDesign::Pad] Pad018
  BaseFeature = -> Pocket024
  Direction = (0,0,-1)
  Length = 2
  Length2 = 10
  Profile = -> Sketch050
  ReferenceAxis = -> Sketch050 [N_Axis]
  Type = 0
FEATURE [Sketcher::SketchObject] Sketch051
  FullyConstrained = true
  MapMode = 5
  Placement = pos=(0,0,39.9391) rot=(0,0,1;0rad)
  Support = -> [Pad018]
FEATURE [PartDesign::Body] Body008  label="MinimalMount"
  BaseFeature = -> Cut001001
  Group = -> [BaseFeature,Sketch040,Pocket017,Sketch041,Pocket018,Sketch042,Pocket019,Sketch043,Pocket020,Sketch044,Pad016,Sketch045,Pocket021,Sketch046,Pad017,Sketch047,Pocket022,Sketch048,Pocket023,Sketch049,Pocket024,Sketch050,Pad018,Sketch051]
  Origin = -> Origin008
  Tip = -> Pad018
FEATURE [PartDesign::Body] Body  label="main_mount"
  Group = -> [Sketch,Pad,Sketch001,Pocket,Sketch002,Pad001,Sketch003,Pad002,Sketch004,Pocket001,Sketch005,Pocket002,Sketch007,Pocket003,Sketch008,Pocket004,Sketch015,Pocket006,Sketch019,Sketch017,Pad004,Pocket007,Sketch020,Pad005,Sketch021,Pocket008,Sketch022,Pocket009,Sketch023,Pocket010,Sketch026,Pad007,Sketch027,Pocket012,Sketch028,Pocket013,Sketch029,Pad008]
  Origin = -> Origin
  Tip = -> Pad008
FEATURE [PartDesign::Pocket] Pocket007
  AllowMultiFace = false
  BaseFeature = -> Pad004
  Direction = (0,0,-1)
  Length = 7
  Length2 = 100
  Profile = -> Sketch017
  Reversed = true
  Type = 0
FEATURE [Sketcher::SketchObject] Sketch019
  FullyConstrained = false
  MapMode = 5
  Placement = pos=(160,0,0) rot=(0.57735,0.57735,0.57735;2.0944rad)
  Support = -> [Pocket007]
  sketch-geometry (2):
    g0: Circle CenterX=100.337 CenterY=-47.9025 CenterZ=0 NormalX=0 NormalY=0 NormalZ=1 AngleXU=0 Radius=51.1849
    g1: Circle CenterX=100.337 CenterY=-47.9025 CenterZ=0 NormalX=0 NormalY=0 NormalZ=1 AngleXU=0 Radius=47.1767
  constraints (1):
    c: Coincident(g1,g0)
FEATURE [PartDesign::Pad] Pad004
  AllowMultiFace = false
  BaseFeature = -> Pocket006
  Direction = (1,0,0)
  Length = 25
  Length2 = 100
  Profile = -> Sketch019
  Type = 0
FEATURE [Sketcher::SketchObject] Sketch020
  FullyConstrained = false
  MapMode = 5
  Placement = pos=(0,0,65) rot=(0,0,1;0rad)
  Support = -> [Pocket007]
  sketch-geometry (1):
    g0: Circle CenterX=100.357 CenterY=-47.855 CenterZ=0 NormalX=0 NormalY=0 NormalZ=1 AngleXU=0 Radius=50.3604
FEATURE [PartDesign::Pad] Pad005
  AllowMultiFace = false
  BaseFeature = -> Pocket007
  Direction = (1,1,1)
  Length = 16
  Length2 = 100
  Profile = -> Sketch020
  Reversed = true
  Type = 0
FEATURE [Sketcher::SketchObject] Sketch021
  FullyConstrained = false
  MapMode = 5
  Placement = pos=(0,0,65) rot=(0,0,1;0rad)
  Support = -> [Pad005]
  sketch-geometry (4):
    g0: LineSegment StartX=-37.9437 StartY=-125.593 StartZ=0 EndX=101.012 EndY=-125.593 EndZ=0
    g1: LineSegment StartX=101.012 StartY=-125.593 StartZ=0 EndX=101.012 EndY=21.4012 EndZ=0
    g2: LineSegment StartX=101.012 StartY=21.4012 StartZ=0 EndX=-33.2351 EndY=21.4012 EndZ=0
    g3: LineSegment StartX=-33.2351 StartY=21.4012 StartZ=0 EndX=-37.9437 EndY=-125.593 EndZ=0
  constraints (7):
    c: Horizontal(g0)
    c: Coincident(g0,g1)
    c: Vertical(g1)
    c: Coincident(g1,g2)
    c: Horizontal(g2)
    c: Coincident(g2,g3)
    c: Coincident(g3,g0)
FEATURE [PartDesign::Pocket] Pocket008
  AllowMultiFace = false
  BaseFeature = -> Pad005
  Direction = (1,1,1)
  Length = 16
  Length2 = 100
  Profile = -> Sketch021
  Type = 0
FEATURE [Sketcher::SketchObject] Sketch022
  FullyConstrained = false
  MapMode = 5
  Placement = pos=(0,0,65) rot=(0,0,1;0rad)
  Support = -> [Pocket008]
  sketch-geometry (1):
    g0: Circle CenterX=101.298 CenterY=-47.7722 CenterZ=0 NormalX=0 NormalY=0 NormalZ=1 AngleXU=0 Radius=21.831
FEATURE [PartDesign::Pocket] Pocket009
  AllowMultiFace = false
  BaseFeature = -> Pocket008
  Direction = (1,1,1)
  Length = 20
  Length2 = 100
  Profile = -> Sketch022
  Type = 0
FEATURE [Sketcher::SketchObject] Sketch023
  FullyConstrained = false
  MapMode = 5
  Placement = pos=(0,0,65) rot=(0,0,1;0rad)
  Support = -> [Pocket009]
  sketch-geometry (5):
    g0: Circle CenterX=124.232 CenterY=-13.5972 CenterZ=0 NormalX=0 NormalY=0 NormalZ=1 AngleXU=0 Radius=3
    g1: Circle CenterX=124.232 CenterY=-81.3884 CenterZ=0 NormalX=0 NormalY=0 NormalZ=1 AngleXU=0 Radius=3
    g2: GeomPoint X=58.7121 Y=14.4068 Z=0
    g3: GeomPoint X=124.232 Y=-81.3884 Z=0
    g4: GeomPoint X=115.277 Y=-5.45373 Z=0
  constraints (4):
    c: Radius(g0) = 3
    c: Equal(g0,g1) = 4.5
    c: Coincident(g3,g1)
    c: Vertical(g1,g0)
FEATURE [PartDesign::Pocket] Pocket010
  AllowMultiFace = false
  BaseFeature = -> Pocket009
  Direction = (1,1,1)
  Length = 0.001
  Length2 = 100
  Profile = -> Sketch023
  Type = 0
FEATURE [Sketcher::SketchObject] Sketch026
  FullyConstrained = false
  MapMode = 5
  Placement = pos=(0,0,0) rot=(1,0,0;3.14159rad)
  Support = -> [Pocket010]
  sketch-geometry (8):
    g0: LineSegment StartX=39.9117 StartY=99.7536 StartZ=0 EndX=160.254 EndY=99.7536 EndZ=0
    g1: LineSegment StartX=160.254 StartY=99.7536 StartZ=0 EndX=160.254 EndY=0.240105 EndZ=0
    g2: LineSegment StartX=160.254 StartY=0.240105 StartZ=0 EndX=39.9117 EndY=0.240105 EndZ=0
    g3: LineSegment StartX=39.9117 StartY=0.240105 StartZ=0 EndX=39.9117 EndY=99.7536 EndZ=0
    g4: LineSegment StartX=53.777 StartY=84.6517 StartZ=0 EndX=146.851 EndY=84.6517 EndZ=0
    g5: LineSegment StartX=146.851 StartY=84.6517 StartZ=0 EndX=146.851 EndY=13.9156 EndZ=0
    g6: LineSegment StartX=146.851 StartY=13.9156 StartZ=0 EndX=53.777 EndY=13.9156 EndZ=0
    g7: LineSegment StartX=53.777 StartY=13.9156 StartZ=0 EndX=53.777 EndY=84.6517 EndZ=0
  constraints (16):
    c: Coincident(g0,g1)
    c: Coincident(g1,g2)
    c: Coincident(g2,g3)
    c: Coincident(g3,g0)
    c: Horizontal(g0)
    c: Horizontal(g2)
    c: Vertical(g1)
    c: Vertical(g3)
    c: Coincident(g4,g5)
    c: Coincident(g5,g6)
    c: Coincident(g6,g7)
    c: Coincident(g7,g4)
    c: Horizontal(g4)
    c: Horizontal(g6)
    c: Vertical(g5)
    c: Vertical(g7)
FEATURE [PartDesign::Pad] Pad007
  AllowMultiFace = false
  BaseFeature = -> Pocket010
  Direction = (1,1,1)
  Length = 15
  Length2 = 100
  Profile = -> Sketch026
  Type = 0
FEATURE [Sketcher::SketchObject] Sketch027
  FullyConstrained = false
  MapMode = 5
  Placement = pos=(0,0,65) rot=(0,0,1;0rad)
  Support = -> [Pad007]
  sketch-geometry (4):
    g0: LineSegment StartX=60.7272 StartY=11.3878 StartZ=0 EndX=133.608 EndY=11.3878 EndZ=0
    g1: LineSegment StartX=133.608 StartY=11.3878 StartZ=0 EndX=133.608 EndY=0.039704 EndZ=0
    g2: LineSegment StartX=133.608 StartY=0.039704 StartZ=0 EndX=60.7272 EndY=0.039704 EndZ=0
    g3: LineSegment StartX=60.7272 StartY=0.039704 StartZ=0 EndX=60.7272 EndY=11.3878 EndZ=0
  constraints (8):
    c: Coincident(g0,g1)
    c: Coincident(g1,g2)
    c: Coincident(g2,g3)
    c: Coincident(g3,g0)
    c: Horizontal(g0)
    c: Horizontal(g2)
    c: Vertical(g1)
    c: Vertical(g3)
FEATURE [PartDesign::Pocket] Pocket012
  AllowMultiFace = false
  BaseFeature = -> Pad007
  Direction = (1,1,1)
  Length = 25
  Length2 = 100
  Profile = -> Sketch027
  Type = 0
FEATURE [Sketcher::SketchObject] Sketch028
  FullyConstrained = false
  MapMode = 5
  Placement = pos=(0,0,0) rot=(1,0,0;3.14159rad)
  Support = -> [Pocket012]
  sketch-geometry (8):
    g0: LineSegment StartX=-12.2554 StartY=72.4585 StartZ=0 EndX=39.8622 EndY=72.4585 EndZ=0
    g1: LineSegment StartX=39.8622 StartY=72.4585 StartZ=0 EndX=39.8622 EndY=31.7237 EndZ=0
    g2: LineSegment StartX=39.8622 StartY=31.7237 StartZ=0 EndX=-12.2554 EndY=31.7237 EndZ=0
    g3: LineSegment StartX=-12.2554 StartY=31.7237 StartZ=0 EndX=-12.2554 EndY=72.4585 EndZ=0
    g4: LineSegment StartX=210.32 StartY=70.3236 StartZ=0 EndX=160.407 EndY=70.3236 EndZ=0
    g5: LineSegment StartX=160.407 StartY=70.3236 StartZ=0 EndX=160.407 EndY=29.7562 EndZ=0
    g6: LineSegment StartX=160.407 StartY=29.7562 StartZ=0 EndX=210.32 EndY=29.7562 EndZ=0
    g7: LineSegment StartX=210.32 StartY=29.7562 StartZ=0 EndX=210.32 EndY=70.3236 EndZ=0
  constraints (16):
    c: Coincident(g0,g1)
    c: Coincident(g1,g2)
    c: Coincident(g2,g3)
    c: Coincident(g3,g0)
    c: Horizontal(g0)
    c: Horizontal(g2)
    c: Vertical(g1)
    c: Vertical(g3)
    c: Coincident(g4,g5)
    c: Coincident(g5,g6)
    c: Coincident(g6,g7)
    c: Coincident(g7,g4)
    c: Horizontal(g4)
    c: Horizontal(g6)
    c: Vertical(g5)
    c: Vertical(g7)
FEATURE [PartDesign::Pocket] Pocket013
  AllowMultiFace = false
  BaseFeature = -> Pocket012
  Direction = (1,1,1)
  Length = 20
  Length2 = 100
  Profile = -> Sketch028
  Type = 0
FEATURE [Sketcher::SketchObject] Sketch029
  FullyConstrained = false
  MapMode = 5
  Placement = pos=(0,0,-15) rot=(1,0,0;3.14159rad)
  Support = -> [Pocket013]
  sketch-geometry (16):
    g0: LineSegment StartX=40.3921 StartY=99.8996 StartZ=0 EndX=7.13215 EndY=99.8996 EndZ=0
    g1: LineSegment StartX=7.13215 StartY=99.8996 StartZ=0 EndX=7.13215 EndY=0.109648 EndZ=0
    g2: LineSegment StartX=7.13215 StartY=0.109648 StartZ=0 EndX=40.3921 EndY=0.109648 EndZ=0
    g3: LineSegment StartX=40.3921 StartY=0.109648 StartZ=0 EndX=40.3921 EndY=99.8996 EndZ=0
    g4: LineSegment StartX=12.5921 StartY=95.3496 StartZ=0 EndX=35.0921 EndY=95.3496 EndZ=0
    g5: LineSegment StartX=35.0921 StartY=95.3496 StartZ=0 EndX=35.0921 EndY=4.02965 EndZ=0
    g6: LineSegment StartX=35.0921 StartY=4.02965 StartZ=0 EndX=12.5921 EndY=4.02965 EndZ=0
    g7: LineSegment StartX=12.5921 StartY=4.02965 StartZ=0 EndX=12.5921 EndY=95.3496 EndZ=0
    g8: LineSegment StartX=192.134 StartY=99.8624 StartZ=0 EndX=158.874 EndY=99.8624 EndZ=0
    g9: LineSegment StartX=158.874 StartY=99.8624 StartZ=0 EndX=158.874 EndY=0.072373 EndZ=0
    g10: LineSegment StartX=158.874 StartY=0.072373 StartZ=0 EndX=192.134 EndY=0.072373 EndZ=0
    g11: LineSegment StartX=192.134 StartY=0.072373 StartZ=0 EndX=192.134 EndY=99.8624 EndZ=0
    g12: LineSegment StartX=164.334 StartY=95.3124 StartZ=0 EndX=186.834 EndY=95.3124 EndZ=0
    g13: LineSegment StartX=186.834 StartY=95.3124 StartZ=0 EndX=186.834 EndY=3.99237 EndZ=0
    g14: LineSegment StartX=186.834 StartY=3.99237 StartZ=0 EndX=164.334 EndY=3.99237 EndZ=0
    g15: LineSegment StartX=164.334 StartY=3.99237 StartZ=0 EndX=164.334 EndY=95.3124 EndZ=0
  constraints (44):
    c: Coincident(g0,g1)
    c: Coincident(g1,g2)
    c: Coincident(g2,g3)
    c: Coincident(g3,g0)
    c: Horizontal(g0)
    c: Horizontal(g2)
    c: Vertical(g1)
    c: Vertical(g3)
    c: DistanceX(g0,g0) = 33.26
    c: DistanceY(g3,g3) = 99.79
    c: Coincident(g4,g5)
    c: Coincident(g5,g6)
    c: Coincident(g6,g7)
    c: Coincident(g7,g4)
    c: Horizontal(g4)
    c: Horizontal(g6)
    c: Vertical(g5)
    c: Vertical(g7)
    c: DistanceX(g4,g4) = 22.5
    c: DistanceY(g5,g5) = 91.32
    c: DistanceX(g1,g6) = 5.46
    c: DistanceY(g1,g6) = 3.92
    c: Coincident(g8,g9)
    c: Coincident(g9,g10)
    c: Coincident(g10,g11)
    c: Coincident(g11,g8)
    c: Horizontal(g8)
    c: Horizontal(g10)
    c: Vertical(g9)
    c: Vertical(g11)
    c: Equal(g0,g8) = 33.26
    c: Equal(g3,g11) = 99.79
    c: Coincident(g12,g13)
    c: Coincident(g13,g14)
    c: Coincident(g14,g15)
    c: Coincident(g15,g12)
    c: Horizontal(g12)
    c: Horizontal(g14)
    c: Vertical(g13)
    c: Vertical(g15)
    c: Equal(g4,g12) = 22.5
    c: Equal(g5,g13) = 91.32
    c: DistanceX(g9,g14) = 5.46
    c: DistanceY(g9,g14) = 3.92
FEATURE [PartDesign::Pad] Pad008
  AllowMultiFace = false
  BaseFeature = -> Pocket013
  Direction = (1,1,1)
  Length = 15
  Length2 = 100
  Profile = -> Sketch029
  Reversed = true
  Type = 0
FEATURE [Part::Cut] Cut
  Base = -> Body
  Tool = -> Body002
FEATURE [Part::Cut] Cut001  label="MainShape"
  Base = -> Cut
  Tool = -> Body003
